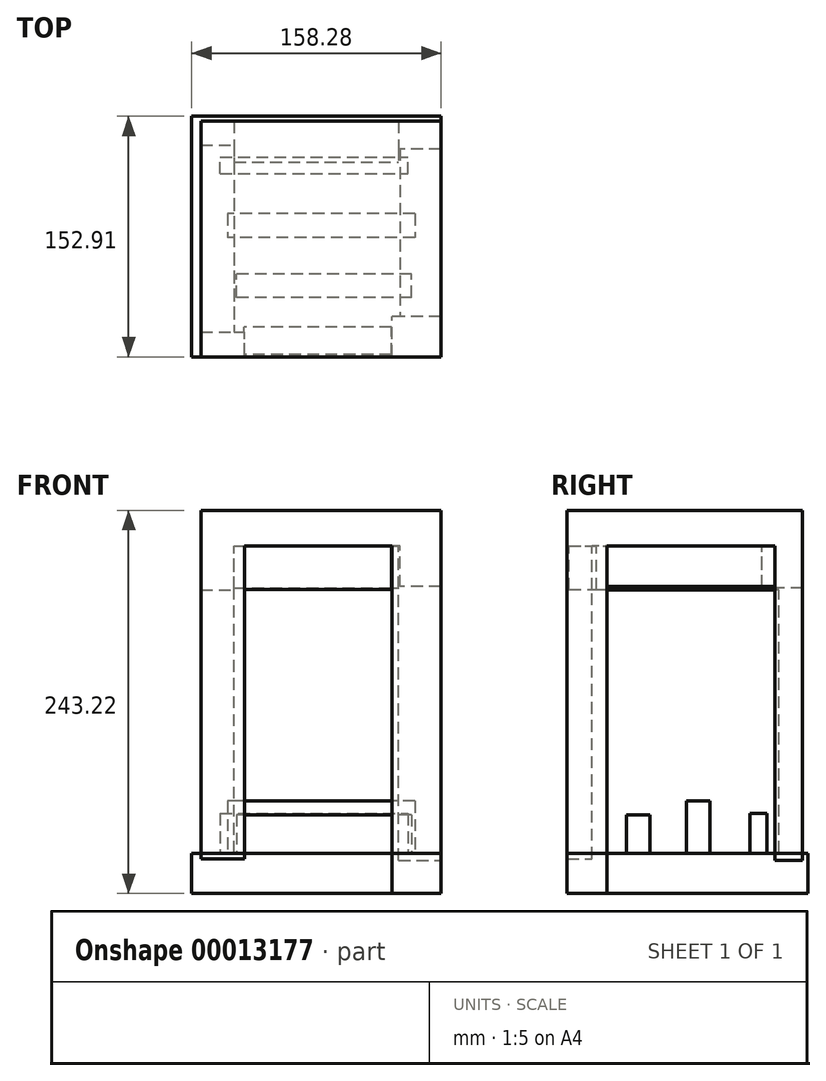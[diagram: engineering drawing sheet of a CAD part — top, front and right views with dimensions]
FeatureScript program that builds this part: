
annotation { "Feature Type Name" : "Feature", "Feature Type Description" : "" }
export const myFeature = defineFeature(function(context is Context, id is Id, definition is map)
    precondition{}
    {
        {
            var Q0;
            Q0=qCreatedBy(makeId("Top.planeOp"),FACE);
            var sketch = newSketch(context, id + "F0", { "sketchPlane" : qUnion([Q0])});
            skLineSegment(sketch, "E0.bottom", {"start": v(-75.16, 73.87) * mm, "end": v(77.34, 73.87) * mm});
            skLineSegment(sketch, "E0.top", {"start": v(-75.16, -75.8) * mm, "end": v(77.34, -75.8) * mm});
            skLineSegment(sketch, "E0.left", {"start": v(-75.16, 73.87) * mm, "end": v(-75.16, -75.8) * mm});
            skLineSegment(sketch, "E0.right", {"start": v(77.34, 73.87) * mm, "end": v(77.34, -75.8) * mm});
            skSolve(sketch);
        }
        {
            var Q0;
            Q0=makeQuery(id+"F0.imprint","IMPRINT",FACE,{"disambiguationData":[TD([[makeQuery(id+"F0.imprint","IMPRINT",EDGE,{"derivedFrom":sQuery(id+"F0.wireOp",EDGE,"E0.bottom")}),-1.0]])]});
            extrude(context, id + "F1", {"entities" : qUnion([Q0]), "depth" : 22.73 * mm});
        }
        {
            var Q0;
            Q0=makeQuery(id+"F1.opExtrude","CAP_FACE",FACE,{"disambiguationData":[OSD([sQuery(id+"F0.wireOp",EDGE,"E0.bottom"),sQuery(id+"F0.wireOp",EDGE,"E0.top"),sQuery(id+"F0.wireOp",EDGE,"E0.left"),sQuery(id+"F0.wireOp",EDGE,"E0.right")])],"isStart":true});
            var sketch = newSketch(context, id + "F2", { "sketchPlane" : qUnion([Q0])});
            skLineSegment(sketch, "E1.bottom", {"start": v(-75.16, -73.87) * mm, "end": v(-54.08, -73.87) * mm});
            skLineSegment(sketch, "E1.top", {"start": v(-75.16, -58.86) * mm, "end": v(-54.08, -58.86) * mm});
            skLineSegment(sketch, "E1.left", {"start": v(-75.16, -73.87) * mm, "end": v(-75.16, -58.86) * mm});
            skLineSegment(sketch, "E1.right", {"start": v(-54.08, -73.87) * mm, "end": v(-54.08, -58.86) * mm});
            skSolve(sketch);
        }
        {
            var Q0;
            Q0=makeQuery(id+"F2.imprint","IMPRINT",FACE,{"disambiguationData":[TD([[makeQuery(id+"F2.imprint","IMPRINT",EDGE,{"derivedFrom":sQuery(id+"F2.wireOp",EDGE,"E1.bottom")}),1.0]])]});
            extrude(context, id + "F3", {"entities" : qUnion([Q0]), "operationType" : NewBodyOperationType.ADD, "depth" : 69.84 * mm});
        }
        {
            var Q0;
            Q0=makeQuery(id+"F1.opExtrude","CAP_FACE",FACE,{"disambiguationData":[OSD([sQuery(id+"F0.wireOp",EDGE,"E0.bottom"),sQuery(id+"F0.wireOp",EDGE,"E0.top"),sQuery(id+"F0.wireOp",EDGE,"E0.left"),sQuery(id+"F0.wireOp",EDGE,"E0.right")])],"isStart":true});
            var sketch = newSketch(context, id + "F4", { "sketchPlane" : qUnion([Q0])});
            skLineSegment(sketch, "E2.bottom", {"start": v(77.34, -73.87) * mm, "end": v(50.38, -73.87) * mm});
            skLineSegment(sketch, "E2.top", {"start": v(77.34, -56.27) * mm, "end": v(50.38, -56.27) * mm});
            skLineSegment(sketch, "E2.left", {"start": v(77.34, -73.87) * mm, "end": v(77.34, -56.27) * mm});
            skLineSegment(sketch, "E2.right", {"start": v(50.38, -73.87) * mm, "end": v(50.38, -56.27) * mm});
            skSolve(sketch);
        }
        {
            var Q0;
            Q0=makeQuery(id+"F4.imprint","IMPRINT",FACE,{"disambiguationData":[TD([[makeQuery(id+"F4.imprint","IMPRINT",EDGE,{"derivedFrom":sQuery(id+"F4.wireOp",EDGE,"E2.bottom")}),1.0]])]});
            extrude(context, id + "F5", {"entities" : qUnion([Q0]), "operationType" : NewBodyOperationType.ADD, "depth" : 79.4 * mm});
        }
        {
            var Q0;
            Q0=makeQuery(id+"F1.opExtrude","CAP_FACE",FACE,{"disambiguationData":[OSD([sQuery(id+"F0.wireOp",EDGE,"E0.bottom"),sQuery(id+"F0.wireOp",EDGE,"E0.top"),sQuery(id+"F0.wireOp",EDGE,"E0.left"),sQuery(id+"F0.wireOp",EDGE,"E0.right")])],"isStart":true});
            var sketch = newSketch(context, id + "F6", { "sketchPlane" : qUnion([Q0])});
            skLineSegment(sketch, "E3.bottom", {"start": v(-75.16, 75.8) * mm, "end": v(-47.33, 75.8) * mm});
            skLineSegment(sketch, "E3.top", {"start": v(-75.16, 59.84) * mm, "end": v(-47.33, 59.84) * mm});
            skLineSegment(sketch, "E3.left", {"start": v(-75.16, 75.8) * mm, "end": v(-75.16, 59.84) * mm});
            skLineSegment(sketch, "E3.right", {"start": v(-47.33, 75.8) * mm, "end": v(-47.33, 59.84) * mm});
            skSolve(sketch);
        }
        {
            var Q0;
            Q0=makeQuery(id+"F6.imprint","IMPRINT",FACE,{"disambiguationData":[TD([[makeQuery(id+"F6.imprint","IMPRINT",EDGE,{"derivedFrom":sQuery(id+"F6.wireOp",EDGE,"E3.bottom")}),-1.0]])]});
            extrude(context, id + "F7", {"entities" : qUnion([Q0]), "operationType" : NewBodyOperationType.ADD, "depth" : 66.02 * mm});
        }
        {
            var Q0;
            Q0=makeQuery(id+"F1.opExtrude","CAP_FACE",FACE,{"disambiguationData":[OSD([sQuery(id+"F0.wireOp",EDGE,"E0.bottom"),sQuery(id+"F0.wireOp",EDGE,"E0.top"),sQuery(id+"F0.wireOp",EDGE,"E0.left"),sQuery(id+"F0.wireOp",EDGE,"E0.right")])],"isStart":true});
            var sketch = newSketch(context, id + "F8", { "sketchPlane" : qUnion([Q0])});
            skLineSegment(sketch, "E4.bottom", {"start": v(77.34, 75.8) * mm, "end": v(46.2, 75.8) * mm});
            skLineSegment(sketch, "E4.top", {"start": v(77.34, 50.25) * mm, "end": v(46.2, 50.25) * mm});
            skLineSegment(sketch, "E4.left", {"start": v(77.34, 75.8) * mm, "end": v(77.34, 50.25) * mm});
            skLineSegment(sketch, "E4.right", {"start": v(46.2, 75.8) * mm, "end": v(46.2, 50.25) * mm});
            skSolve(sketch);
        }
        {
            var Q0;
            Q0=makeQuery(id+"F8.imprint","IMPRINT",FACE,{"disambiguationData":[TD([[makeQuery(id+"F8.imprint","IMPRINT",EDGE,{"derivedFrom":sQuery(id+"F8.wireOp",EDGE,"E4.bottom")}),-1.0]])]});
            extrude(context, id + "F9", {"entities" : qUnion([Q0]), "operationType" : NewBodyOperationType.ADD, "depth" : 90.65 * mm});
        }
        {
            var Q0;
            Q0=makeQuery(id+"F7.opExtrude","CAP_FACE",FACE,{"disambiguationData":[OSD([sQuery(id+"F6.wireOp",EDGE,"E3.bottom"),sQuery(id+"F6.wireOp",EDGE,"E3.top"),sQuery(id+"F6.wireOp",EDGE,"E3.left"),sQuery(id+"F6.wireOp",EDGE,"E3.right")])],"isStart":false});
            extrude(context, id + "F10", {"entities" : qUnion([Q0]), "operationType" : NewBodyOperationType.ADD, "depth" : 33.5 * mm});
        }
        {
            var Q0;
            Q0=makeQuery(id+"F1.opExtrude","CAP_FACE",FACE,{"disambiguationData":[OSD([sQuery(id+"F0.wireOp",EDGE,"E0.bottom"),sQuery(id+"F0.wireOp",EDGE,"E0.top"),sQuery(id+"F0.wireOp",EDGE,"E0.left"),sQuery(id+"F0.wireOp",EDGE,"E0.right")])],"isStart":true});
            var sketch = newSketch(context, id + "F11", { "sketchPlane" : qUnion([Q0])});
            skLineSegment(sketch, "E5.bottom", {"start": v(-54.08, -58.86) * mm, "end": v(-75.16, -58.86) * mm});
            skLineSegment(sketch, "E5.top", {"start": v(-54.08, 59.84) * mm, "end": v(-75.16, 59.84) * mm});
            skLineSegment(sketch, "E5.left", {"start": v(-54.08, -58.86) * mm, "end": v(-54.08, 59.84) * mm});
            skLineSegment(sketch, "E5.right", {"start": v(-75.16, -58.86) * mm, "end": v(-75.16, 59.84) * mm});
            skSolve(sketch);
        }
        {
            var Q0;
            Q0=makeQuery(id+"F11.imprint","IMPRINT",FACE,{"disambiguationData":[TD([[makeQuery(id+"F11.imprint","IMPRINT",EDGE,{"derivedFrom":sQuery(id+"F11.wireOp",EDGE,"E5.bottom")}),1.0]])]});
            extrude(context, id + "F12", {"entities" : qUnion([Q0]), "operationType" : NewBodyOperationType.ADD, "depth" : 27.74 * mm});
        }
        {
            var Q0;
            Q0=makeQuery(id+"F1.opExtrude","CAP_FACE",FACE,{"disambiguationData":[OSD([sQuery(id+"F0.wireOp",EDGE,"E0.bottom"),sQuery(id+"F0.wireOp",EDGE,"E0.top"),sQuery(id+"F0.wireOp",EDGE,"E0.left"),sQuery(id+"F0.wireOp",EDGE,"E0.right")])],"isStart":true});
            var sketch = newSketch(context, id + "F13", { "sketchPlane" : qUnion([Q0])});
            skLineSegment(sketch, "E6.bottom", {"start": v(-54.08, -73.87) * mm, "end": v(50.38, -73.87) * mm});
            skLineSegment(sketch, "E6.top", {"start": v(-54.08, -48.1) * mm, "end": v(50.38, -48.1) * mm});
            skLineSegment(sketch, "E6.left", {"start": v(-54.08, -73.87) * mm, "end": v(-54.08, -48.1) * mm});
            skLineSegment(sketch, "E6.right", {"start": v(50.38, -73.87) * mm, "end": v(50.38, -48.1) * mm});
            skSolve(sketch);
        }
        {
            var Q0;
            {var subQ3=sQuery(id+"F13.wireOp",EDGE,"E6.bottom");Q0=makeQuery(id+"F13.imprint","IMPRINT",FACE,{"disambiguationData":[TD([[makeQuery(id+"F13.imprint","IMPRINT",EDGE,{"derivedFrom":subQ3}),1.0]])]});}
            extrude(context, id + "F14", {"entities" : qUnion([Q0]), "operationType" : NewBodyOperationType.ADD, "depth" : 26.64 * mm});
        }
        {
            var Q0;
            Q0=makeQuery(id+"F5.opExtrude","CAP_FACE",FACE,{"disambiguationData":[OSD([sQuery(id+"F4.wireOp",EDGE,"E2.bottom"),sQuery(id+"F4.wireOp",EDGE,"E2.top"),sQuery(id+"F4.wireOp",EDGE,"E2.left"),sQuery(id+"F4.wireOp",EDGE,"E2.right")])],"isStart":false});
            extrude(context, id + "F15", {"entities" : qUnion([Q0]), "operationType" : NewBodyOperationType.ADD, "depth" : 4.97 * mm});
        }
        {
            var Q0;
            Q0=makeQuery(id+"F3.opExtrude","CAP_FACE",FACE,{"disambiguationData":[OSD([sQuery(id+"F2.wireOp",EDGE,"E1.bottom"),sQuery(id+"F2.wireOp",EDGE,"E1.top"),sQuery(id+"F2.wireOp",EDGE,"E1.left"),sQuery(id+"F2.wireOp",EDGE,"E1.right")])],"isStart":false});
            extrude(context, id + "F16", {"entities" : qUnion([Q0]), "operationType" : NewBodyOperationType.ADD, "depth" : 27.6 * mm});
        }
        {
            var Q0;
            {var subQ5=sQuery(id+"F2.wireOp",EDGE,"E1.top");Q0=makeQuery(id+"F2.imprint","IMPRINT",FACE,{"disambiguationData":[TD([[makeQuery(id+"F2.imprint","IMPRINT",EDGE,{"derivedFrom":subQ5}),1.0]])]});}
            var sketch = newSketch(context, id + "F17", { "sketchPlane" : qUnion([Q0])});
            skLineSegment(sketch, "E7.bottom", {"start": v(51.32, -56.92) * mm, "end": v(77.28, -56.92) * mm});
            skLineSegment(sketch, "E7.top", {"start": v(51.32, 50.55) * mm, "end": v(77.28, 50.55) * mm});
            skLineSegment(sketch, "E7.left", {"start": v(51.32, -56.92) * mm, "end": v(51.32, 50.55) * mm});
            skLineSegment(sketch, "E7.right", {"start": v(77.28, -56.92) * mm, "end": v(77.28, 50.55) * mm});
            skSolve(sketch);
        }
        {
            var Q0;
            Q0=makeQuery(id+"F17.imprint","IMPRINT",FACE,{"disambiguationData":[TD([[makeQuery(id+"F17.imprint","IMPRINT",EDGE,{"derivedFrom":sQuery(id+"F17.wireOp",EDGE,"E7.bottom")}),1.0]])]});
            extrude(context, id + "F18", {"entities" : qUnion([Q0]), "operationType" : NewBodyOperationType.ADD, "depth" : 25.62 * mm});
        }
        {
            var Q0;
            {var subQ5=sQuery(id+"F2.wireOp",EDGE,"E1.top");Q0=makeQuery(id+"F2.imprint","IMPRINT",FACE,{"disambiguationData":[TD([[makeQuery(id+"F2.imprint","IMPRINT",EDGE,{"derivedFrom":subQ5}),1.0]])]});}
            var sketch = newSketch(context, id + "F19", { "sketchPlane" : qUnion([Q0])});
            skLineSegment(sketch, "E8.bottom", {"start": v(45.94, 74.35) * mm, "end": v(-47.73, 74.35) * mm});
            skLineSegment(sketch, "E8.top", {"start": v(45.94, 56.94) * mm, "end": v(-47.73, 56.94) * mm});
            skLineSegment(sketch, "E8.left", {"start": v(45.94, 74.35) * mm, "end": v(45.94, 56.94) * mm});
            skLineSegment(sketch, "E8.right", {"start": v(-47.73, 74.35) * mm, "end": v(-47.73, 56.94) * mm});
            skSolve(sketch);
        }
        {
            var Q0;
            Q0=makeQuery(id+"F19.imprint","IMPRINT",FACE,{"disambiguationData":[TD([[makeQuery(id+"F19.imprint","IMPRINT",EDGE,{"derivedFrom":sQuery(id+"F19.wireOp",EDGE,"E8.bottom")}),1.0]])]});
            extrude(context, id + "F20", {"entities" : qUnion([Q0]), "operationType" : NewBodyOperationType.ADD, "depth" : 27.6 * mm});
        }
        {
            var Q0;
            Q0=makeQuery(id+"F9.opExtrude","CAP_FACE",FACE,{"disambiguationData":[OSD([sQuery(id+"F8.wireOp",EDGE,"E4.bottom"),sQuery(id+"F8.wireOp",EDGE,"E4.top"),sQuery(id+"F8.wireOp",EDGE,"E4.left"),sQuery(id+"F8.wireOp",EDGE,"E4.right")])],"isStart":false});
            var sketch = newSketch(context, id + "F21", { "sketchPlane" : qUnion([Q0])});
            skLineSegment(sketch, "E9.bottom", {"start": v(46.2, 50.25) * mm, "end": v(77.34, 50.25) * mm});
            skLineSegment(sketch, "E9.top", {"start": v(46.2, 75.8) * mm, "end": v(77.34, 75.8) * mm});
            skLineSegment(sketch, "E9.left", {"start": v(46.2, 50.25) * mm, "end": v(46.2, 75.8) * mm});
            skLineSegment(sketch, "E9.right", {"start": v(77.34, 50.25) * mm, "end": v(77.34, 75.8) * mm});
            skSolve(sketch);
        }
        {
            var Q0;
            Q0=makeQuery(id+"F21.imprint","IMPRINT",FACE,{"disambiguationData":[TD([[makeQuery(id+"F21.imprint","IMPRINT",EDGE,{"derivedFrom":sQuery(id+"F21.wireOp",EDGE,"E9.bottom")}),-1.0]])]});
            extrude(context, id + "F22", {"entities" : qUnion([Q0]), "operationType" : NewBodyOperationType.ADD, "depth" : 104.44 * mm});
        }
        {
            var Q0;
            Q0=makeQuery(id+"F10.opExtrude","CAP_FACE",FACE,{"disambiguationData":[OSD([sQuery(id+"F6.wireOp",EDGE,"E3.bottom"),sQuery(id+"F6.wireOp",EDGE,"E3.top"),sQuery(id+"F6.wireOp",EDGE,"E3.left"),sQuery(id+"F6.wireOp",EDGE,"E3.right")])],"isStart":false});
            extrude(context, id + "F23", {"entities" : qUnion([Q0]), "operationType" : NewBodyOperationType.ADD, "depth" : 65.66 * mm});
        }
        {
            var Q0;
            Q0=makeQuery(id+"F23.opExtrude","CAP_FACE",FACE,{"disambiguationData":[OSD([sQuery(id+"F6.wireOp",EDGE,"E3.bottom"),sQuery(id+"F6.wireOp",EDGE,"E3.top"),sQuery(id+"F6.wireOp",EDGE,"E3.left"),sQuery(id+"F6.wireOp",EDGE,"E3.right")])],"isStart":false});
            extrude(context, id + "F24", {"entities" : qUnion([Q0]), "operationType" : NewBodyOperationType.ADD, "depth" : 33.3 * mm});
        }
        {
            var Q0;
            Q0=makeQuery(id+"F15.opExtrude","CAP_FACE",FACE,{"disambiguationData":[OSD([sQuery(id+"F4.wireOp",EDGE,"E2.bottom"),sQuery(id+"F4.wireOp",EDGE,"E2.top"),sQuery(id+"F4.wireOp",EDGE,"E2.left"),sQuery(id+"F4.wireOp",EDGE,"E2.right")])],"isStart":false});
            extrude(context, id + "F25", {"entities" : qUnion([Q0]), "operationType" : NewBodyOperationType.ADD, "depth" : 115.15 * mm});
        }
        {
            var Q0;
            Q0=makeQuery(id+"F16.opExtrude","CAP_FACE",FACE,{"disambiguationData":[OSD([sQuery(id+"F2.wireOp",EDGE,"E1.bottom"),sQuery(id+"F2.wireOp",EDGE,"E1.top"),sQuery(id+"F2.wireOp",EDGE,"E1.left"),sQuery(id+"F2.wireOp",EDGE,"E1.right")])],"isStart":false});
            extrude(context, id + "F26", {"entities" : qUnion([Q0]), "operationType" : NewBodyOperationType.ADD, "depth" : 97.35 * mm});
        }
        {
            var Q0;
            Q0=makeQuery(id+"F20.opExtrude","CAP_FACE",FACE,{"disambiguationData":[OSD([sQuery(id+"F19.wireOp",EDGE,"E8.bottom"),sQuery(id+"F19.wireOp",EDGE,"E8.top"),sQuery(id+"F19.wireOp",EDGE,"E8.left"),sQuery(id+"F19.wireOp",EDGE,"E8.right")])],"isStart":false});
            var sketch = newSketch(context, id + "F27", { "sketchPlane" : qUnion([Q0])});
            skLineSegment(sketch, "E10.bottom", {"start": v(45.94, 65.65) * mm, "end": v(-47.33, 65.65) * mm});
            skLineSegment(sketch, "E10.top", {"start": v(45.94, 74.35) * mm, "end": v(-47.33, 74.35) * mm});
            skLineSegment(sketch, "E10.left", {"start": v(45.94, 65.65) * mm, "end": v(45.94, 74.35) * mm});
            skLineSegment(sketch, "E10.right", {"start": v(-47.33, 65.65) * mm, "end": v(-47.33, 74.35) * mm});
            skSolve(sketch);
        }
        {
            var Q0;
            Q0=sQuery(id+"F27.wireOp",EDGE,"E10.top");
            extrude(context, id + "F28", {"bodyType" : ToolBodyType.SURFACE, "surfaceEntities" : qUnion([Q0]), "depth" : 166.03 * mm});
        }
        {
            var Q0;
            Q0=makeQuery(id+"F22.opExtrude","CAP_FACE",FACE,{"disambiguationData":[OSD([sQuery(id+"F21.wireOp",EDGE,"E9.bottom"),sQuery(id+"F21.wireOp",EDGE,"E9.top"),sQuery(id+"F21.wireOp",EDGE,"E9.left"),sQuery(id+"F21.wireOp",EDGE,"E9.right")])],"isStart":false});
            var sketch = newSketch(context, id + "F29", { "sketchPlane" : qUnion([Q0])});
            skLineSegment(sketch, "E11.bottom", {"start": v(77.34, 75.8) * mm, "end": v(-80.94, 75.8) * mm});
            skLineSegment(sketch, "E11.top", {"start": v(77.34, -77.1) * mm, "end": v(-80.94, -77.1) * mm});
            skLineSegment(sketch, "E11.left", {"start": v(77.34, 75.8) * mm, "end": v(77.34, -77.1) * mm});
            skLineSegment(sketch, "E11.right", {"start": v(-80.94, 75.8) * mm, "end": v(-80.94, -77.1) * mm});
            skSolve(sketch);
        }
        {
            var Q0;
            {var subQ3=sQuery(id+"F29.wireOp",EDGE,"E11.top");Q0=makeQuery(id+"F29.imprint","IMPRINT",FACE,{"disambiguationData":[TD([[makeQuery(id+"F29.imprint","IMPRINT",EDGE,{"derivedFrom":subQ3}),-1.0]])]});}
            extrude(context, id + "F30", {"entities" : qUnion([Q0]), "depth" : 25.4 * mm});
        }
        {
            var Q0;
            Q0=makeQuery(id+"F22.opExtrude","CAP_FACE",FACE,{"disambiguationData":[OSD([sQuery(id+"F21.wireOp",EDGE,"E9.bottom"),sQuery(id+"F21.wireOp",EDGE,"E9.top"),sQuery(id+"F21.wireOp",EDGE,"E9.left"),sQuery(id+"F21.wireOp",EDGE,"E9.right")])],"isStart":false});
            extrude(context, id + "F31", {"entities" : qUnion([Q0]), "depth" : 25.4 * mm});
        }
        {
            var Q0;
            Q0=makeQuery(id+"F30.opExtrude","CAP_FACE",FACE,{"disambiguationData":[OSD([sQuery(id+"F21.wireOp",EDGE,"E9.bottom"),sQuery(id+"F21.wireOp",EDGE,"E9.left"),sQuery(id+"F29.wireOp",EDGE,"E11.bottom"),sQuery(id+"F29.wireOp",EDGE,"E11.top"),sQuery(id+"F29.wireOp",EDGE,"E11.left"),sQuery(id+"F29.wireOp",EDGE,"E11.right")])],"isStart":true});
            var sketch = newSketch(context, id + "F32", { "sketchPlane" : qUnion([Q0])});
            skLineSegment(sketch, "E12.bottom", {"start": v(60.85, 15.1) * mm, "end": v(-58.12, 15.1) * mm});
            skLineSegment(sketch, "E12.top", {"start": v(60.85, 0) * mm, "end": v(-58.12, 0) * mm});
            skLineSegment(sketch, "E12.left", {"start": v(60.85, 15.1) * mm, "end": v(60.85, 0) * mm});
            skLineSegment(sketch, "E12.right", {"start": v(-58.12, 15.1) * mm, "end": v(-58.12, 0) * mm});
            skSolve(sketch);
        }
        {
            var Q0;
            Q0=makeQuery(id+"F32.imprint","IMPRINT",FACE,{"disambiguationData":[TD([[makeQuery(id+"F32.imprint","IMPRINT",EDGE,{"derivedFrom":sQuery(id+"F32.wireOp",EDGE,"E12.bottom")}),1.0]])]});
            extrude(context, id + "F33", {"entities" : qUnion([Q0]), "operationType" : NewBodyOperationType.ADD, "depth" : 33.17 * mm});
        }
        {
            var Q0;
            Q0=makeQuery(id+"F30.opExtrude","CAP_FACE",FACE,{"disambiguationData":[OSD([sQuery(id+"F21.wireOp",EDGE,"E9.bottom"),sQuery(id+"F21.wireOp",EDGE,"E9.left"),sQuery(id+"F29.wireOp",EDGE,"E11.bottom"),sQuery(id+"F29.wireOp",EDGE,"E11.top"),sQuery(id+"F29.wireOp",EDGE,"E11.left"),sQuery(id+"F29.wireOp",EDGE,"E11.right")])],"isStart":true});
            var sketch = newSketch(context, id + "F34", { "sketchPlane" : qUnion([Q0])});
            skLineSegment(sketch, "E13.bottom", {"start": v(58.6, -38.01) * mm, "end": v(-52.39, -38.01) * mm});
            skLineSegment(sketch, "E13.top", {"start": v(58.6, -23.05) * mm, "end": v(-52.39, -23.05) * mm});
            skLineSegment(sketch, "E13.left", {"start": v(58.6, -38.01) * mm, "end": v(58.6, -23.05) * mm});
            skLineSegment(sketch, "E13.right", {"start": v(-52.39, -38.01) * mm, "end": v(-52.39, -23.05) * mm});
            skSolve(sketch);
        }
        {
            var Q0;
            Q0=makeQuery(id+"F34.imprint","IMPRINT",FACE,{"disambiguationData":[TD([[makeQuery(id+"F34.imprint","IMPRINT",EDGE,{"derivedFrom":sQuery(id+"F34.wireOp",EDGE,"E13.bottom")}),-1.0]])]});
            extrude(context, id + "F35", {"entities" : qUnion([Q0]), "operationType" : NewBodyOperationType.ADD, "depth" : 24.53 * mm});
        }
        {
            var Q0;
            Q0=makeQuery(id+"F30.opExtrude","CAP_FACE",FACE,{"disambiguationData":[OSD([sQuery(id+"F21.wireOp",EDGE,"E9.bottom"),sQuery(id+"F21.wireOp",EDGE,"E9.left"),sQuery(id+"F29.wireOp",EDGE,"E11.bottom"),sQuery(id+"F29.wireOp",EDGE,"E11.top"),sQuery(id+"F29.wireOp",EDGE,"E11.left"),sQuery(id+"F29.wireOp",EDGE,"E11.right")])],"isStart":true});
            var sketch = newSketch(context, id + "F36", { "sketchPlane" : qUnion([Q0])});
            skLineSegment(sketch, "E14.bottom", {"start": v(-62.93, 40.55) * mm, "end": v(56.46, 40.55) * mm});
            skLineSegment(sketch, "E14.top", {"start": v(-62.93, 51.12) * mm, "end": v(56.46, 51.12) * mm});
            skLineSegment(sketch, "E14.left", {"start": v(-62.93, 40.55) * mm, "end": v(-62.93, 51.12) * mm});
            skLineSegment(sketch, "E14.right", {"start": v(56.46, 40.55) * mm, "end": v(56.46, 51.12) * mm});
            skSolve(sketch);
        }
        {
            var Q0;
            Q0=makeQuery(id+"F36.imprint","IMPRINT",FACE,{"disambiguationData":[TD([[makeQuery(id+"F36.imprint","IMPRINT",EDGE,{"derivedFrom":sQuery(id+"F36.wireOp",EDGE,"E14.bottom")}),1.0]])]});
            extrude(context, id + "F37", {"entities" : qUnion([Q0]), "operationType" : NewBodyOperationType.ADD, "depth" : 25.4 * mm});
        }
    });
